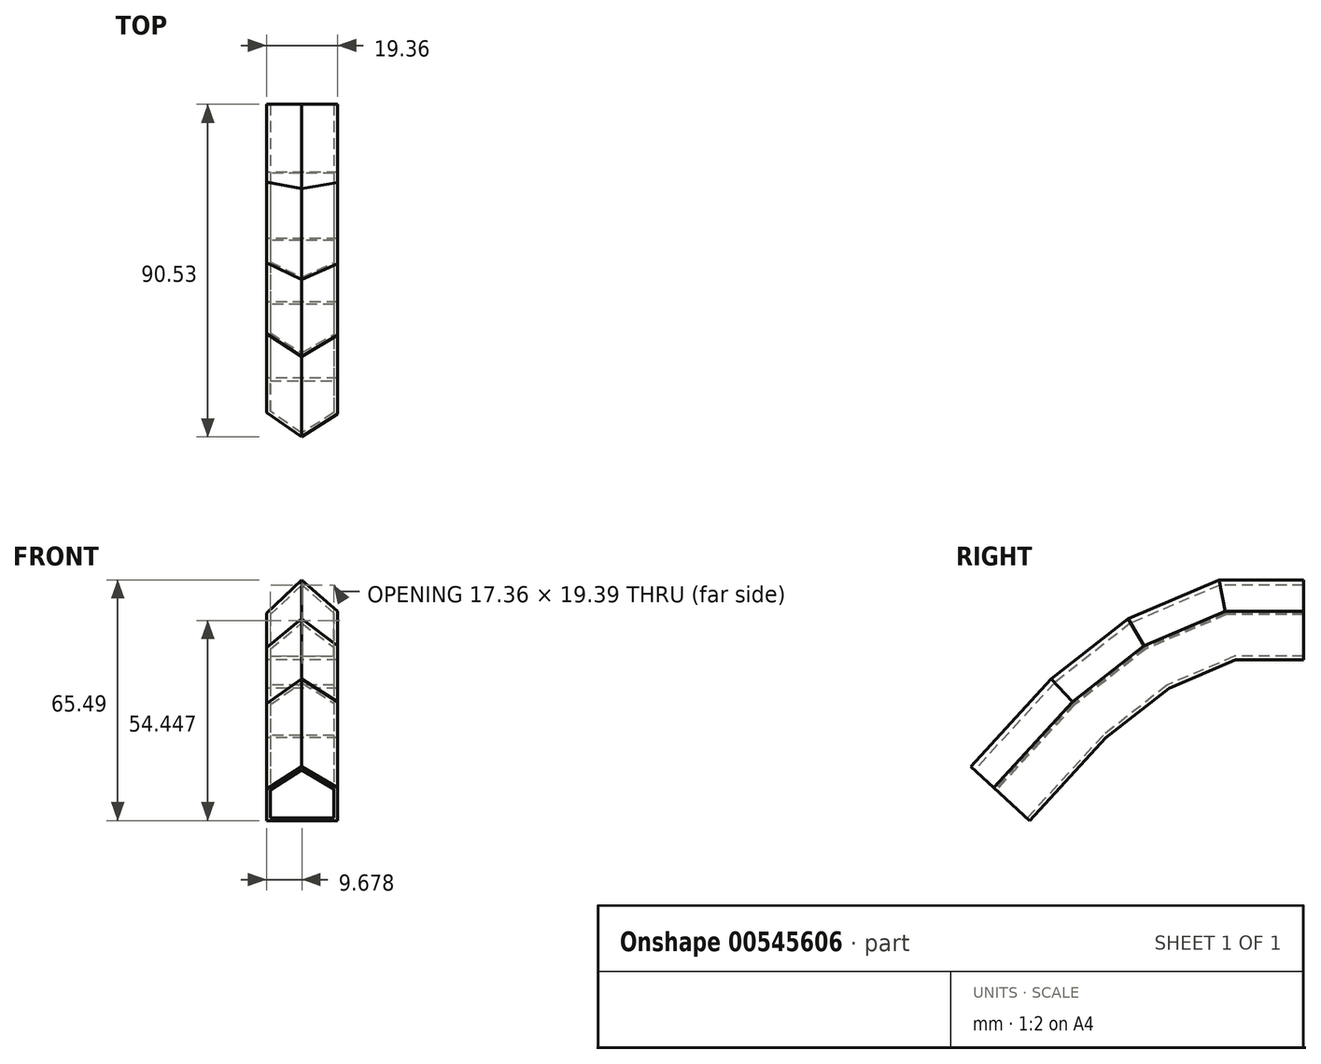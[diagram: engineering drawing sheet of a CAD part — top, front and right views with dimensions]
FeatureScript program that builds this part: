
annotation { "Feature Type Name" : "Feature", "Feature Type Description" : "" }
export const myFeature = defineFeature(function(context is Context, id is Id, definition is map)
    precondition{}
    {
        {
            var Q0;
            Q0=qCreatedBy(makeId("Front.planeOp"),FACE);
            var sketch = newSketch(context, id + "F0", { "sketchPlane" : qUnion([Q0])});
            skLineSegment(sketch, "E0", {"start": v(0, 0) * mm, "end": v(0, 12.73) * mm});
            skLineSegment(sketch, "E1", {"start": v(0, 12.73) * mm, "end": v(9.55, 21.74) * mm});
            skLineSegment(sketch, "E2", {"start": v(9.55, 0) * mm, "end": v(0, 0) * mm});
            skLineSegment(sketch, "E3", {"start": v(9.55, 0) * mm, "end": v(19.36, 0) * mm});
            skLineSegment(sketch, "E4", {"start": v(19.36, 0) * mm, "end": v(19.36, 13.26) * mm});
            skLineSegment(sketch, "E5", {"start": v(19.36, 13.26) * mm, "end": v(9.55, 21.74) * mm});
            skSolve(sketch);
        }
        {
            var Q0;
            Q0=qCreatedBy(makeId("Right.planeOp"),FACE);
            var sketch = newSketch(context, id + "F1", { "sketchPlane" : qUnion([Q0])});
            skLineSegment(sketch, "E6", {"start": v(0, 0) * mm, "end": v(-18.56, 0) * mm});
            skLineSegment(sketch, "E7", {"start": v(-18.56, 0) * mm, "end": v(-36.6, -7.69) * mm});
            skLineSegment(sketch, "E8", {"start": v(-36.6, -7.69) * mm, "end": v(-53.83, -21.21) * mm});
            skLineSegment(sketch, "E9", {"start": v(-53.83, -21.21) * mm, "end": v(-74.5, -43.75) * mm});
            skSolve(sketch);
        }
        {
            var Q0;
            Q0=makeQuery(id+"F0.imprint","IMPRINT",FACE,{"disambiguationData":[TD([[makeQuery(id+"F0.imprint","IMPRINT",EDGE,{"derivedFrom":sQuery(id+"F0.wireOp",EDGE,"E0")}),-1.0]])]});
            var Q1;
            Q1=sQuery(id+"F1.wireOp",EDGE,"E6");
            var Q2;
            Q2=sQuery(id+"F1.wireOp",EDGE,"E7");
            var Q3;
            Q3=sQuery(id+"F1.wireOp",EDGE,"E8");
            var Q4;
            Q4=sQuery(id+"F1.wireOp",EDGE,"E9");
            sweep(context, id + "F2", {"profiles" : qUnion([Q0]), "path" : qUnion([Q1, Q2, Q3, Q4])});
        }
        {
            var Q0;
            Q0=makeQuery(id+"F2.opSweep","CAP_FACE",FACE,{"disambiguationData":[OSD([sQuery(id+"F0.wireOp",EDGE,"E0"),sQuery(id+"F0.wireOp",EDGE,"E1"),sQuery(id+"F0.wireOp",EDGE,"E2"),sQuery(id+"F0.wireOp",EDGE,"E3"),sQuery(id+"F0.wireOp",EDGE,"E4"),sQuery(id+"F0.wireOp",EDGE,"E5"),sQuery(id+"F1.wireOp",VERTEX,"E6.start")])],"isStart":true});
            var Q1;
            Q1=makeQuery(id+"F2.opSweep","CAP_FACE",FACE,{"disambiguationData":[OSD([sQuery(id+"F0.wireOp",EDGE,"E0"),sQuery(id+"F0.wireOp",EDGE,"E1"),sQuery(id+"F0.wireOp",EDGE,"E2"),sQuery(id+"F0.wireOp",EDGE,"E3"),sQuery(id+"F0.wireOp",EDGE,"E4"),sQuery(id+"F0.wireOp",EDGE,"E5"),sQuery(id+"F1.wireOp",VERTEX,"E9.end")])],"isStart":false});
            shell(context, id + "F3", {"entities" : qUnion([Q0, Q1]), "thickness" : 1 * mm});
        }
    });
